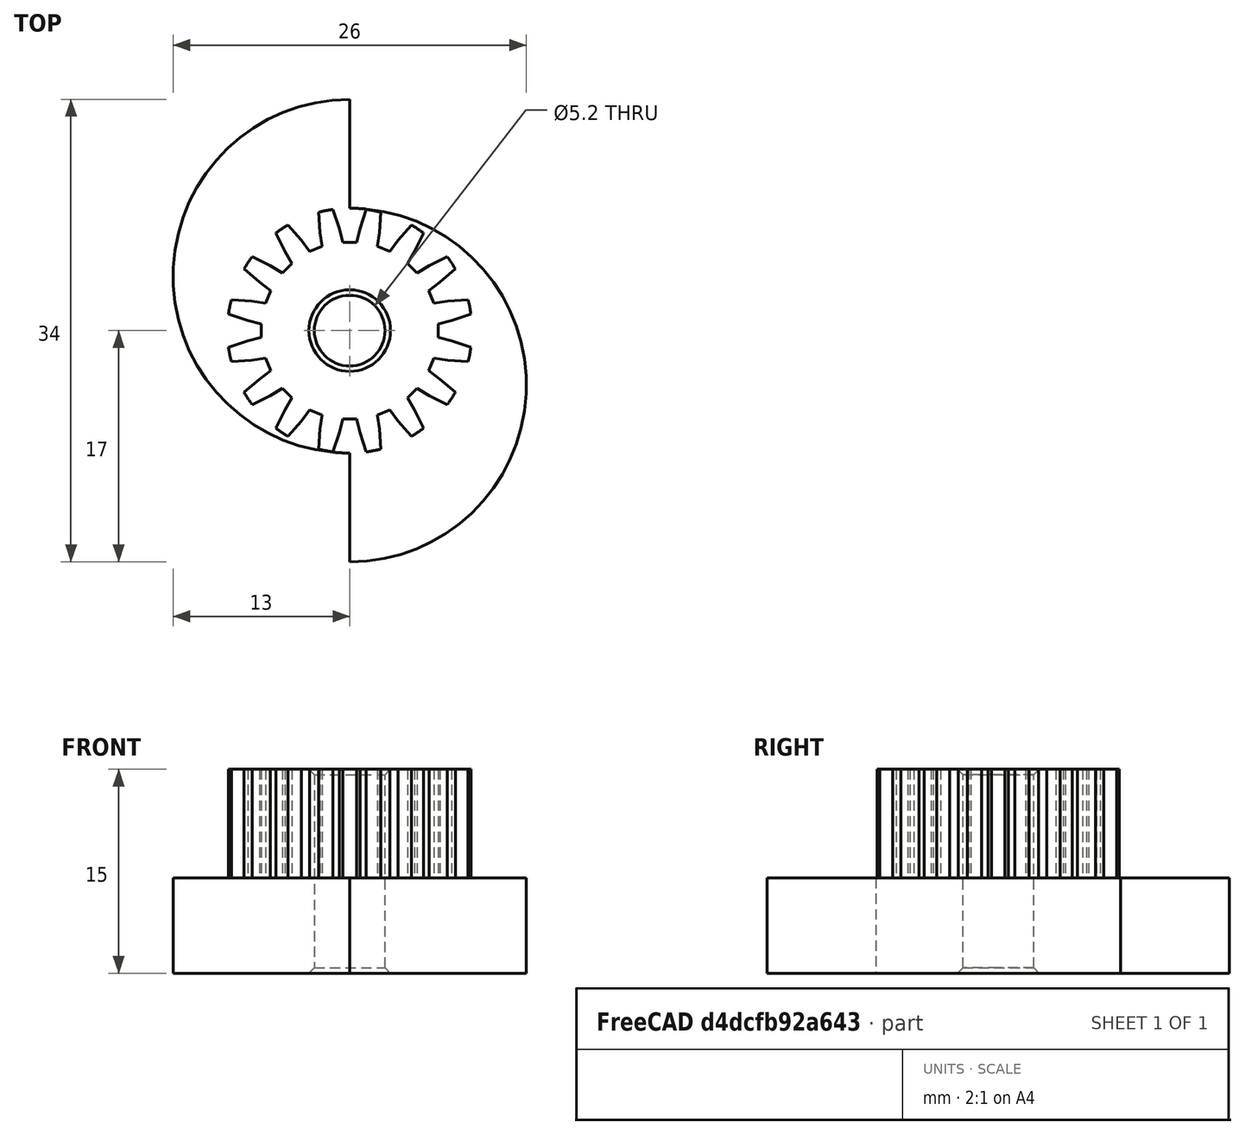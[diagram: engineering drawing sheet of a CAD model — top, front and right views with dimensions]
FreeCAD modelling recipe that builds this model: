
FCSTD DOCUMENT  (FreeCAD 0.18R4 (GitTag))
Label: Stepper_Motor_Wheel_2
License: All rights reserved
LicenseURL: http://en.wikipedia.org/wiki/All_rights_reserved
objects: Sketcher::SketchObject×4, PartDesign::Pocket×3, PartDesign::PolarPattern×2, PartDesign::Revolution×1, PartDesign::Chamfer×1, PartDesign::Body×1
note: 16 computed .brp shape members not serialized (recipe doc carries the construction recipe); baked Part::Feature solids carry a one-line shape summary decoded from their .brp

FEATURE [Sketcher::SketchObject] Sketch
  MapMode = 5
  Placement = pos=(0,0,0) rot=(1,0,0;1.5708rad)
  Support = -> [XZ_Plane]
  sketch-geometry (6):
    g0: LineSegment StartX=0 StartY=0 StartZ=0 EndX=17 EndY=0 EndZ=0
    g1: LineSegment StartX=17 StartY=0 StartZ=0 EndX=17 EndY=7 EndZ=0
    g2: LineSegment StartX=17 StartY=7 StartZ=0 EndX=9 EndY=7 EndZ=0
    g3: LineSegment StartX=9 StartY=7 StartZ=0 EndX=9 EndY=15 EndZ=0
    g4: LineSegment StartX=9 StartY=15 StartZ=0 EndX=0 EndY=15 EndZ=0
    g5: LineSegment StartX=0 StartY=15 StartZ=0 EndX=0 EndY=0 EndZ=0
  constraints (17):
    c: Coincident(g-1,g0)
    c: PointOnObject(g0,g-1)
    c: Coincident(g0,g1)
    c: Vertical(g1)
    c: Coincident(g1,g2)
    c: Horizontal(g2)
    c: Coincident(g2,g3)
    c: Vertical(g3)
    c: Coincident(g3,g4)
    c: Horizontal(g4)
    c: PointOnObject(g4,g-2)
    c: DistanceX(g0,g0) = 17
    c: DistanceY(g1,g1) = 7
    c: DistanceY(g3,g3) = 8
    c: DistanceX(g4,g4) = 9
    c: Coincident(g5,g4)
    c: Coincident(g5,g0)
FEATURE [PartDesign::Revolution] Revolution
  Angle = 360
  Axis = (0,2e-16,1)
  Base = (0,0,0)
  Placement = pos=(0,0,0) rot=(1,0,0;1.5708rad)
  Profile = -> Sketch
  ReferenceAxis = -> Sketch [V_Axis]
  Refine = true
  Reversed = true
FEATURE [Sketcher::SketchObject] Sketch001
  ExternalGeometry = -> [Revolution]
  MapMode = 5
  Placement = pos=(0,4.7e-15,7) rot=(0,0,1;3.14159rad)
  Support = -> [Revolution]
  sketch-geometry (5):
    g0: LineSegment StartX=0 StartY=17 StartZ=0 EndX=17 EndY=17 EndZ=0
    g1: LineSegment StartX=0 StartY=17 StartZ=0 EndX=8.6175e-12 EndY=9 EndZ=0
    g2: ArcOfCircle CenterX=0 CenterY=-4 CenterZ=0 NormalX=0 NormalY=0 NormalZ=1 AngleXU=0 Radius=13 StartAngle=4.71239 EndAngle=7.85398
    g3: LineSegment StartX=17 StartY=17 StartZ=0 EndX=17 EndY=-17 EndZ=0
    g4: LineSegment StartX=17 StartY=-17 StartZ=0 EndX=0 EndY=-17 EndZ=0
  constraints (16):
    c: PointOnObject(g0,g-2)
    c: Horizontal(g0)
    c: Coincident(g1,g0)
    c: PointOnObject(g1,g-2)
    c: Coincident(g2,g1)
    c: PointOnObject(g0,g-3)
    c: PointOnObject(g2,g-3)
    c: PointOnObject(g2,g-2)
    c: DistanceY(g1,g1) = 8
    c: Coincident(g0,g3)
    c: Vertical(g3)
    c: Coincident(g3,g4)
    c: Coincident(g4,g2)
    c: Horizontal(g4)
    c: Tangent(g3,g-3)
    c: PointOnObject(g2,g-2)
FEATURE [PartDesign::Pocket] Pocket
  BaseFeature = -> Revolution
  Length = 7
  Length2 = 100
  Placement = pos=(0,0,0) rot=(1,0,0;1.5708rad)
  Profile = -> Sketch001
  Refine = true
  Type = 0
FEATURE [PartDesign::PolarPattern] PolarPattern
  Angle = 360
  Axis = -> Sketch001 [N_Axis]
  BaseFeature = -> Pocket
  Occurrences = 2
  Originals = -> [Pocket]
  Placement = pos=(0,0,0) rot=(1,0,0;1.5708rad)
  Refine = true
FEATURE [Sketcher::SketchObject] Sketch002
  ExternalGeometry = -> [Revolution]
  MapMode = 5
  Placement = pos=(0,1e-14,15) rot=(0,0,1;3.14159rad)
  Support = -> [Revolution]
  sketch-geometry (6):
    g0: LineSegment StartX=-1.25 StartY=9 StartZ=0 EndX=1.25 EndY=9 EndZ=0
    g1: LineSegment StartX=1.25 StartY=9 StartZ=0 EndX=0.75 EndY=7.5 EndZ=0
    g2: LineSegment StartX=0.75 StartY=7.5 StartZ=0 EndX=0.5 EndY=6.5 EndZ=0
    g3: LineSegment StartX=0.5 StartY=6.5 StartZ=0 EndX=-0.5 EndY=6.5 EndZ=0
    g4: LineSegment StartX=-0.5 StartY=6.5 StartZ=0 EndX=-0.75 EndY=7.5 EndZ=0
    g5: LineSegment StartX=-0.75 StartY=7.5 StartZ=0 EndX=-1.25 EndY=9 EndZ=0
  constraints (15):
    c: Coincident(g0,g1)
    c: Coincident(g1,g2)
    c: Coincident(g2,g3)
    c: Coincident(g3,g4)
    c: Coincident(g4,g5)
    c: Coincident(g5,g0)
    c: Symmetric(g0,g0,g-2)
    c: Symmetric(g3,g2,g-2)
    c: DistanceX(g3,g3) = 1
    c: DistanceX(g4,g1) = 1.5
    c: Symmetric(g4,g1,g-2)
    c: DistanceY(g2,g1) = 1
    c: DistanceY(g2,g0) = 2.5
    c: DistanceX(g0,g0) = 2.5
    c: Tangent(g0,g-3)
FEATURE [PartDesign::Pocket] Pocket001
  BaseFeature = -> PolarPattern
  Length = 8
  Length2 = 100
  Placement = pos=(0,0,0) rot=(1,0,0;1.5708rad)
  Profile = -> Sketch002
  Refine = true
  Type = 0
FEATURE [PartDesign::PolarPattern] PolarPattern001
  Angle = 360
  Axis = -> Sketch002 [N_Axis]
  BaseFeature = -> Pocket001
  Occurrences = 16
  Originals = -> [Pocket001]
  Placement = pos=(0,0,0) rot=(1,0,0;1.5708rad)
  Refine = true
FEATURE [Sketcher::SketchObject] Sketch003
  MapMode = 5
  Placement = pos=(0,1e-14,15) rot=(0,0,1;3.14159rad)
  Support = -> [Revolution]
  sketch-geometry (1):
    g0: Circle CenterX=0 CenterY=0 CenterZ=0 NormalX=0 NormalY=0 NormalZ=1 AngleXU=0 Radius=2.6
  constraints (2):
    c: Coincident(g0,g-1)
    c: Radius(g0) = 2.6
FEATURE [PartDesign::Pocket] Pocket002
  BaseFeature = -> PolarPattern001
  Length = 15
  Length2 = 100
  Placement = pos=(0,0,0) rot=(1,0,0;1.5708rad)
  Profile = -> Sketch003
  Refine = true
  Type = 0
FEATURE [PartDesign::Chamfer] Chamfer
  Base = -> Pocket002 [Face6]
  BaseFeature = -> Pocket002
  Placement = pos=(0,0,0) rot=(1,0,0;1.5708rad)
  Size = 0.4
FEATURE [PartDesign::Body] Body
  Group = -> [Sketch,Revolution,Sketch001,Pocket,PolarPattern,Sketch002,Pocket001,PolarPattern001,Sketch003,Pocket002,Chamfer]
  Origin = -> Origin
  Tip = -> Chamfer
